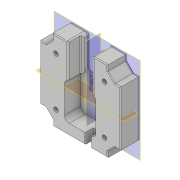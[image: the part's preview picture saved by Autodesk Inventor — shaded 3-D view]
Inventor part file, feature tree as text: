
AUTODESK INVENTOR PART (.ipt)
format: ipt  version: 2022 (Build 260153000, 153)  size: 428,544 bytes
history: native  units: mm
features: reference x17, other x10, sketch x9, extrude x8, plane x5, projected_geometry x4, fillet x2, chamfer x1, hole x1
ambient origin geometry x8: Origin, YZ Plane, XZ Plane, XY Plane, X Axis, Y Axis, Z Axis, Center Point
bodies: Solid1 (feature_tree)
feature tree (57):
  plane  "Work Plane1"
  extrude  "Extrusion1"  Depth=53.8mm
  extrude  "IM_offset"  Depth=53.8mm
  plane  "Arbeitsebene5"
  plane  "Arbeitsebene6"
  extrude  "Extrusion26"  Depth=45.0mm
  chamfer  "Fase2"  Distance=0.1mm
  plane  "Arbeitsebene9"
  extrude  "Extrusion29"  Depth=2.0mm
  extrude  "Extrusion30"  Depth=2.0mm
  sketch  "Skizze36"  dims[d32=2.8mm]
  plane  "Arbeitsebene10"
  extrude  "Extrusion31"  Depth=2.0mm
  fillet  "Rundung3"  Radius=0.2mm
  hole  "Bohrung2"  [1 undecoded]
  extrude  "Extrusion32"  Depth=2.0mm
  extrude  "Extrusion33"  Depth=10.0mm TaperAngle=0.0deg
  fillet  "Rundung4"  Radius=2.0mm
  sketch  "Sketch1"  dims[d10=12.0mm d11=0.0mm d18=53.8mm]
  reference  "Reference1"
  reference  "Reference2"
  reference  "Reference3"
  reference  "Reference4"
  reference  "Reference9"
  reference  "Reference20"
  reference  "Reference21"
  reference  "Reference22"
  reference  "Reference23"
  reference  "Reference24"
  sketch  "Skizze4"  dims[d19=45.0deg d20=53.8mm]
  projected_geometry  "Projizierte Kontur1"
  sketch  "Skizze31"  dims[d21=45.0mm d22=45.0mm]
  projected_geometry  "Projizierte Kontur17"
  sketch  "Skizze34"  dims[d30=20.0mm]
  reference  "Referenz35"
  sketch  "Skizze35"  dims[d31=20.0mm]
  reference  "Referenz36"
  reference  "Referenz37"
  reference  "Referenz38"
  reference  "Referenz39"
  reference  "Referenz40"
  sketch  "Skizze37"  dims[d33=2.8mm]
  projected_geometry  "Projizierte Kontur18"
  reference  "Referenz41"
  sketch  "Skizze38"  dims[d34=2.8mm]
  projected_geometry  "Projizierte Kontur19"
  sketch  "Skizze39"  dims[d35=3.0mm d36=0.1mm d37=0.1mm d38=0.1mm d39=0.1mm d40=0.2mm d41=10.0mm d42=0.0mm d181=7.5mm d182=10.0mm d183=0.0mm d184=0.5mm d185=2.0mm d186=45.0deg d193=-1.5mm d194=8.6mm d195=8.6mm d196=0.0mm d197=0.0mm d198=10.0mm d199=0.0mm d200=4.0mm d201=12.0mm d202=0.0mm d203=1.0mm d204=30.0mm d205=30.0mm d206=2.8mm d207=6.0mm d208=8.0mm d209=6.0mm d210=90.0deg d211=8.0mm d212=20.594885mm d213=4.0mm d214=5.0mm d215=0.0mm d216=0.0mm d217=0.0mm d218=2.0mm d160=0.5mm d161=0.872665mm d162=0.5mm d163=0.872665mm]
  other  "Assembly_Cube_v2_Thorlabs.iam"
  other  "10_Cube_Base:1"
  other  "00_Base_v0:1"
  other  "Assembly_Cube_Kinematic_Mirrormount_v2.iam"
  other  "Assembly_Cube_empty_1x1_v2:1"
  other  "10_Cube_1x1_v2:1"
  other  "10_Lid_1x1_v2:1"
  other  "Assembly_Cube_SEEED_Xiao_Sense_Camera_v3.iam"
  other  "00_Seeeduino Xiao:1"
  other  "10_Cube_Lid:1"
note: 1 required parameter value undecoded (feature->parameter linkage not recoverable at this tier; creation-order binding heuristic only, values carry confidence <= 0.55)
